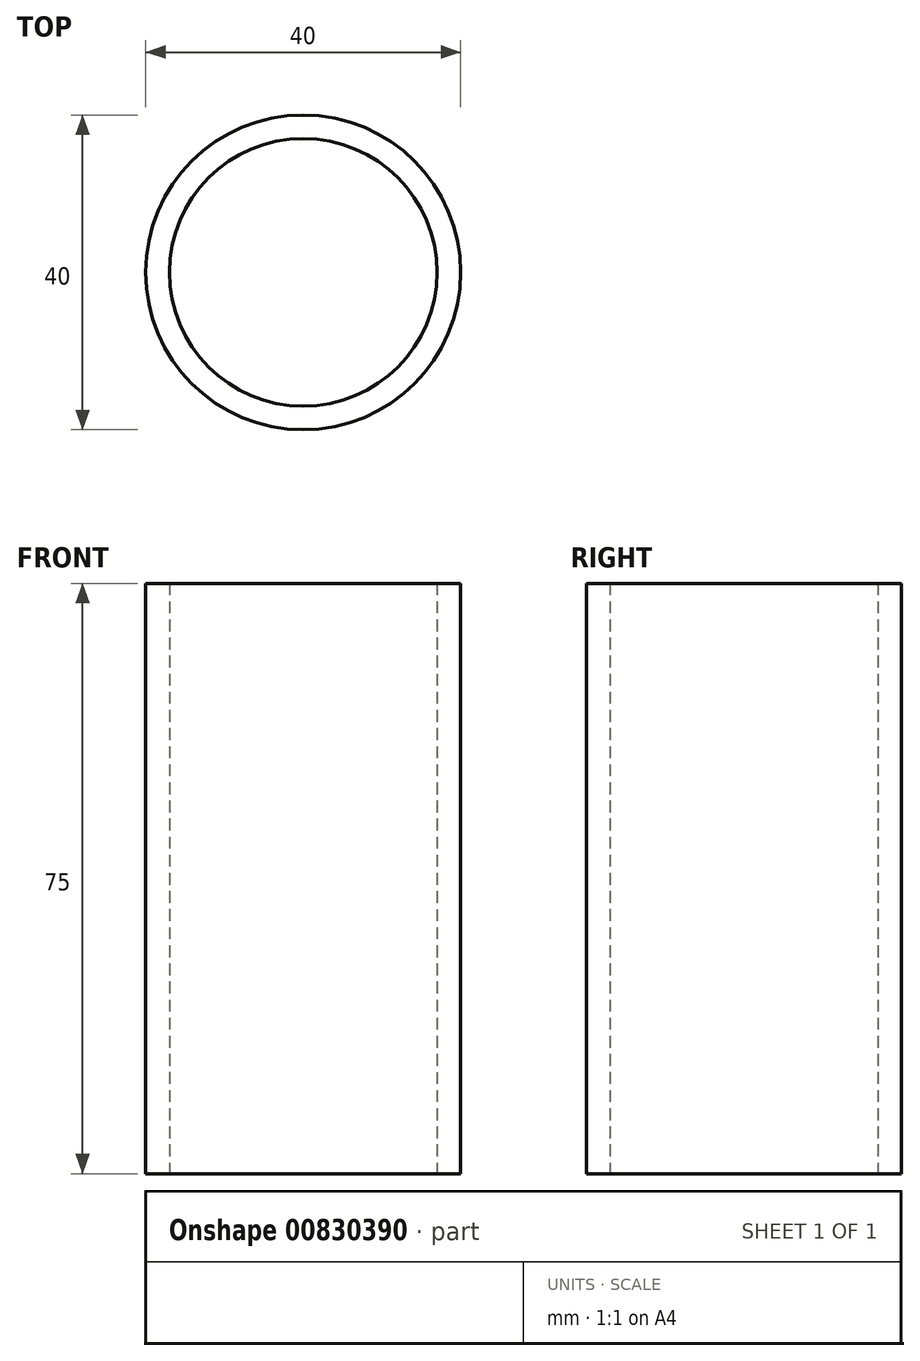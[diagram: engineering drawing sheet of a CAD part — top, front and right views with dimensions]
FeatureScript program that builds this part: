
annotation { "Feature Type Name" : "Feature", "Feature Type Description" : "" }
export const myFeature = defineFeature(function(context is Context, id is Id, definition is map)
    precondition{}
    {
        {
            var Q0;
            Q0=qCreatedBy(makeId("Top.planeOp"),FACE);
            var sketch = newSketch(context, id + "F0", { "sketchPlane" : qUnion([Q0])});
            skCircle(sketch, "E0", {"center": v(0, 0) * mm, "radius": 20 * mm});
            skCircle(sketch, "E1.0", {"center": v(0, 0) * mm, "radius": 17 * mm});
            skSolve(sketch);
        }
        {
            var Q0;
            Q0 = qSketchRegion(id + "F0", true);
            extrude(context, id + "F1", {"entities" : qUnion([Q0]), "depth" : 75 * mm, "offsetDistance" : 25 * mm});
        }
    });
